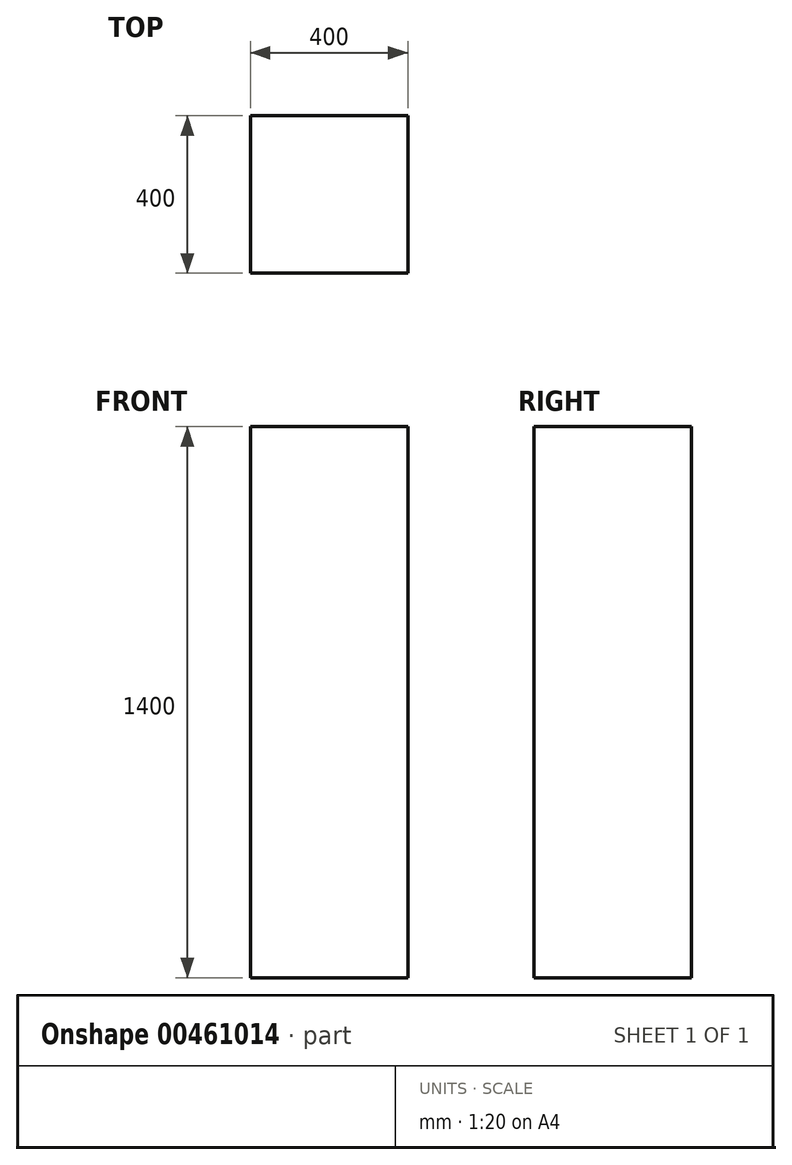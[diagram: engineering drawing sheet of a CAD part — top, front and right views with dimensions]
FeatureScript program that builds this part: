
annotation { "Feature Type Name" : "Feature", "Feature Type Description" : "" }
export const myFeature = defineFeature(function(context is Context, id is Id, definition is map)
    precondition{}
    {
        {
            var Q0;
            Q0=qCreatedBy(makeId("Top.planeOp"),FACE);
            var sketch = newSketch(context, id + "F0", { "sketchPlane" : qUnion([Q0])});
            skLineSegment(sketch, "E0.bottom", {"start": v(0, 0) * mm, "end": v(400, 0) * mm});
            skLineSegment(sketch, "E0.top", {"start": v(0, -400) * mm, "end": v(400, -400) * mm});
            skLineSegment(sketch, "E0.left", {"start": v(0, 0) * mm, "end": v(0, -400) * mm});
            skLineSegment(sketch, "E0.right", {"start": v(400, 0) * mm, "end": v(400, -400) * mm});
            skSolve(sketch);
        }
        {
            var Q0;
            Q0=makeQuery(id+"F0.imprint","IMPRINT",FACE,{"disambiguationData":[TD([[makeQuery(id+"F0.imprint","IMPRINT",EDGE,{"derivedFrom":sQuery(id+"F0.wireOp",EDGE,"E0.bottom")}),-1.0]])]});
            extrude(context, id + "F1", {"entities" : qUnion([Q0]), "depth" : 1400 * mm});
        }
    });
